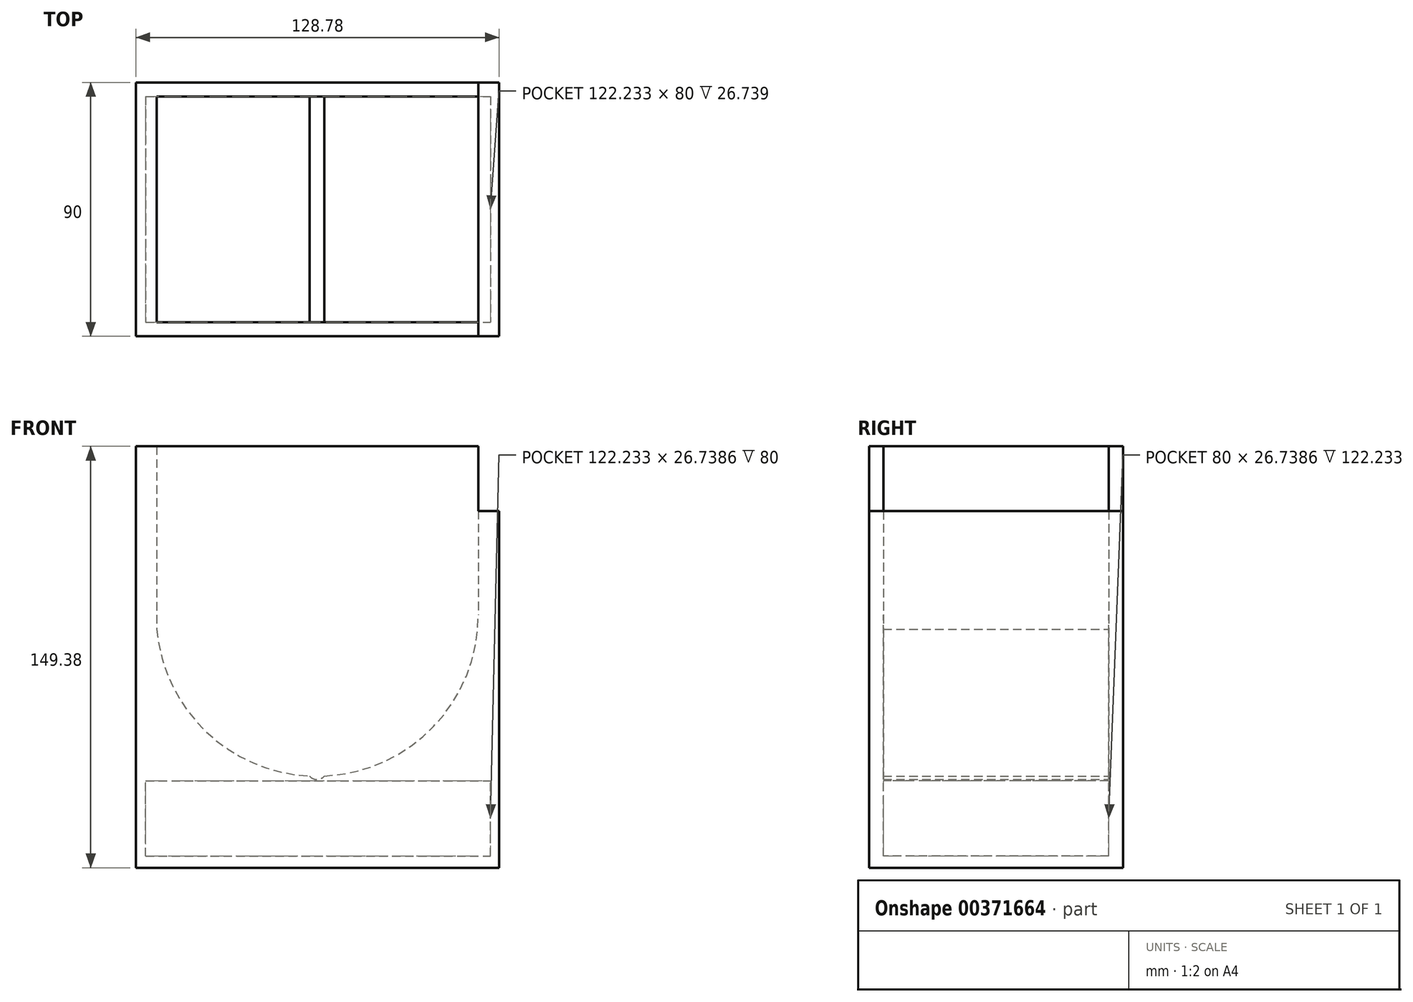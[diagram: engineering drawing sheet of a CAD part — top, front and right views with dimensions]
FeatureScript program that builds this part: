
annotation { "Feature Type Name" : "Feature", "Feature Type Description" : "" }
export const myFeature = defineFeature(function(context is Context, id is Id, definition is map)
    precondition{}
    {
        {
            var Q0;
            Q0=qCreatedBy(makeId("Front.planeOp"),FACE);
            var sketch = newSketch(context, id + "F0", { "sketchPlane" : qUnion([Q0])});
            skLineSegment(sketch, "E0", {"start": v(-64.39, 75) * mm, "end": v(-64.39, -74.37) * mm});
            skLineSegment(sketch, "E1", {"start": v(-64.39, 75) * mm, "end": v(-57, 75) * mm});
            skLineSegment(sketch, "E2", {"start": v(-57, 75) * mm, "end": v(-57, 10.19) * mm});
            skLineSegment(sketch, "E3", {"start": v(-64.39, -74.37) * mm, "end": v(0, -74.37) * mm});
            skLineSegment(sketch, "E4.MirrorCS", {"start": v(64.39, -74.37) * mm, "end": v(0, -74.37) * mm});
            skLineSegment(sketch, "E5.MirrorCS", {"start": v(64.39, 52.13) * mm, "end": v(57, 52.13) * mm});
            skLineSegment(sketch, "E6.MirrorCS", {"start": v(64.39, 52.13) * mm, "end": v(64.39, -74.37) * mm});
            skLineSegment(sketch, "E7.MirrorCS", {"start": v(57, 52.13) * mm, "end": v(57, 15.2) * mm});
            skArc(sketch, "E8", {"start": v(-57, 10.19) * mm, "mid": v(2.4, -41.85) * mm, "end": v(57, 15.2) * mm});
            skLineSegment(sketch, "E9", {"start": v(57, 75) * mm, "end": v(57, 52.13) * mm});
            skLineSegment(sketch, "E10.bottom", {"start": v(-60.93, -70.26) * mm, "end": v(61.3, -70.26) * mm});
            skLineSegment(sketch, "E10.top", {"start": v(-60.93, -43.52) * mm, "end": v(61.3, -43.52) * mm});
            skLineSegment(sketch, "E10.left", {"start": v(-60.93, -70.26) * mm, "end": v(-60.93, -43.52) * mm});
            skLineSegment(sketch, "E10.right", {"start": v(61.3, -70.26) * mm, "end": v(61.3, -43.52) * mm});
            skLineSegment(sketch, "E11", {"start": v(-57, 75) * mm, "end": v(57, 75) * mm});
            skArc(sketch, "E12", {"start": v(-2.82, -41.85) * mm, "mid": v(-0.21, -43.1) * mm, "end": v(2.4, -41.85) * mm});
            skSolve(sketch);
        }
        {
            var Q0;
            Q0=makeQuery(id+"F0.imprint","IMPRINT",FACE,{"disambiguationData":[TD([[makeQuery(id+"F0.imprint","IMPRINT",EDGE,{"derivedFrom":sQuery(id+"F0.wireOp",EDGE,"E0")}),1.0]])]});
            var Q1;
            {var subQ4=sQuery(id+"F0.wireOp",EDGE,"E2");Q1=makeQuery(id+"F0.imprint","IMPRINT",FACE,{"disambiguationData":[TD([[makeQuery(id+"F0.imprint","IMPRINT",EDGE,{"derivedFrom":subQ4}),1.0]])]});}
            var Q2;
            Q2=makeQuery(id+"F0.imprint","IMPRINT",FACE,{"disambiguationData":[TD([[makeQuery(id+"F0.imprint","IMPRINT",EDGE,{"derivedFrom":sQuery(id+"F0.wireOp",EDGE,"E10.bottom")}),1.0]])]});
            var Q3;
            {var subQ0=sQuery(id+"F0.wireOp",EDGE,"E12");Q3=makeQuery(id+"F0.imprint","IMPRINT",FACE,{"disambiguationData":[TD([[makeQuery(id+"F0.imprint","IMPRINT",EDGE,{"derivedFrom":subQ0}),1.0]])]});}
            extrude(context, id + "F1", {"entities" : qUnion([Q0, Q1, Q2, Q3]), "depth" : 90 * mm, "symmetric" : true});
        }
        {
            var Q0;
            {var subQ4=sQuery(id+"F0.wireOp",EDGE,"E2");Q0=makeQuery(id+"F0.imprint","IMPRINT",FACE,{"disambiguationData":[TD([[makeQuery(id+"F0.imprint","IMPRINT",EDGE,{"derivedFrom":subQ4}),1.0]])]});}
            var Q1;
            {var subQ0=sQuery(id+"F0.wireOp",EDGE,"E12");Q1=makeQuery(id+"F0.imprint","IMPRINT",FACE,{"disambiguationData":[TD([[makeQuery(id+"F0.imprint","IMPRINT",EDGE,{"derivedFrom":subQ0}),1.0]])]});}
            extrude(context, id + "F2", {"entities" : qUnion([Q0, Q1]), "operationType" : NewBodyOperationType.REMOVE, "depth" : 80 * mm, "symmetric" : true});
        }
        {
            var Q0;
            Q0=makeQuery(id+"F0.imprint","IMPRINT",FACE,{"disambiguationData":[TD([[makeQuery(id+"F0.imprint","IMPRINT",EDGE,{"derivedFrom":sQuery(id+"F0.wireOp",EDGE,"E10.bottom")}),1.0]])]});
            extrude(context, id + "F3", {"entities" : qUnion([Q0]), "operationType" : NewBodyOperationType.REMOVE, "oppositeDirection" : true, "depth" : 80 * mm, "symmetric" : true});
        }
    });
